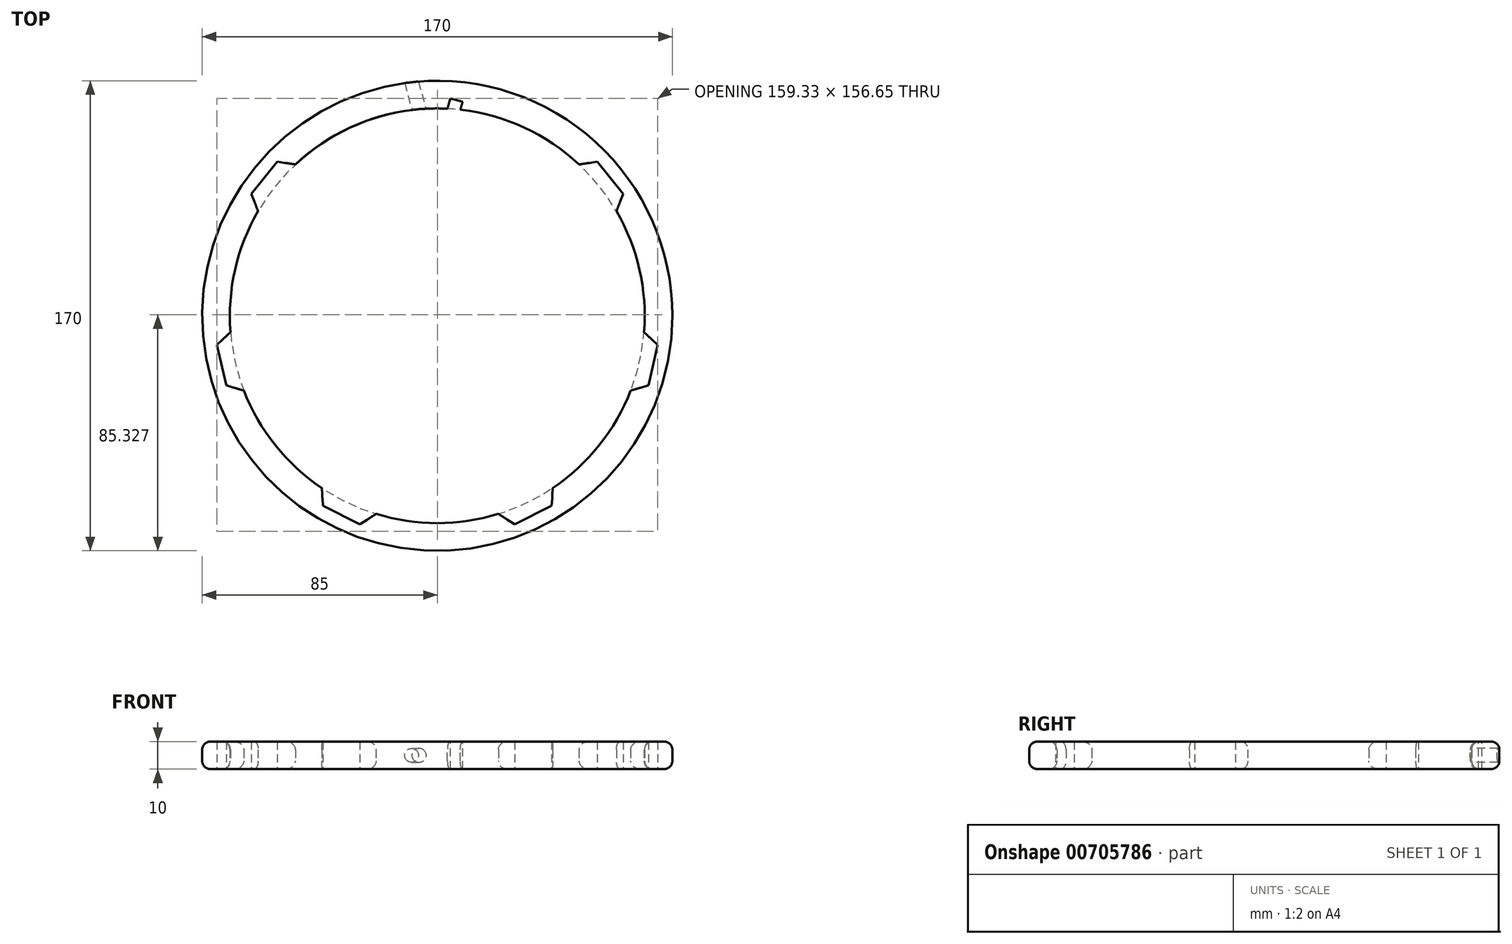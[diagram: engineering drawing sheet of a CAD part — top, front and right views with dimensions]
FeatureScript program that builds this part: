
annotation { "Feature Type Name" : "Feature", "Feature Type Description" : "" }
export const myFeature = defineFeature(function(context is Context, id is Id, definition is map)
    precondition{}
    {
        {
            var Q0;
            Q0=qCreatedBy(makeId("Top.planeOp"),FACE);
            var sketch = newSketch(context, id + "F0", { "sketchPlane" : qUnion([Q0])});
            skCircle(sketch, "E0", {"center": v(0, 0) * mm, "radius": 85 * mm});
            skCircle(sketch, "E1.0", {"center": v(0, 0) * mm, "radius": 75 * mm});
            skPoint(sketch, "E2", {"position": v(0, 80) * mm});
            skPoint(sketch, "E3.1.1", {"position": v(-62.55, 49.88) * mm});
            skPoint(sketch, "E3.2.1", {"position": v(-78, -17.8) * mm});
            skPoint(sketch, "E3.3.1", {"position": v(-34.71, -72.08) * mm});
            skPoint(sketch, "E3.4.1", {"position": v(34.71, -72.08) * mm});
            skPoint(sketch, "E3.5.1", {"position": v(78, -17.8) * mm});
            skPoint(sketch, "E3.6.1", {"position": v(62.55, 49.88) * mm});
            skPoint(sketch, "E4", {"position": v(-7.48, 80) * mm});
            skPoint(sketch, "E5.MirrorP", {"position": v(7.48, 80) * mm});
            skLineSegment(sketch, "E6", {"start": v(-7.48, 80) * mm, "end": v(34.71, -72.08) * mm, "construction": true});
            skLineSegment(sketch, "E7", {"start": v(34.71, -72.08) * mm, "end": v(-62.55, 49.88) * mm, "construction": true});
            skLineSegment(sketch, "E8", {"start": v(-62.55, 49.88) * mm, "end": v(78, -17.8) * mm, "construction": true});
            skLineSegment(sketch, "E9", {"start": v(78, -17.8) * mm, "end": v(-78, -17.8) * mm, "construction": true});
            skLineSegment(sketch, "E10", {"start": v(-78, -17.8) * mm, "end": v(62.55, 49.88) * mm, "construction": true});
            skLineSegment(sketch, "E11", {"start": v(62.55, 49.88) * mm, "end": v(-34.71, -72.08) * mm, "construction": true});
            skLineSegment(sketch, "E12", {"start": v(-34.71, -72.08) * mm, "end": v(7.48, 80) * mm, "construction": true});
            skCircle(sketch, "E13", {"center": v(34.71, -72.08) * mm, "radius": 23.6 * mm, "construction": true});
            skCircle(sketch, "E14", {"center": v(78, -17.8) * mm, "radius": 25.74 * mm, "construction": true});
            skLineSegment(sketch, "E15", {"start": v(54.8, -6.63) * mm, "end": v(52.26, -17.8) * mm, "construction": true});
            skLineSegment(sketch, "E16", {"start": v(76.33, -25.11) * mm, "end": v(79.66, -10.49) * mm});
            skLineSegment(sketch, "E17", {"start": v(57.87, 55.74) * mm, "end": v(67.22, 44.02) * mm});
            skCircle(sketch, "E18", {"center": v(62.55, 49.88) * mm, "radius": 21.8 * mm, "construction": true});
            skLineSegment(sketch, "E19", {"start": v(48.95, 32.83) * mm, "end": v(42.9, 40.42) * mm, "construction": true});
            skLineSegment(sketch, "E20", {"start": v(78, -17.8) * mm, "end": v(55.94, -12.77) * mm, "construction": true});
            skLineSegment(sketch, "E21", {"start": v(79.66, -10.49) * mm, "end": v(74.76, -5.94) * mm});
            skLineSegment(sketch, "E22.MirrorCS", {"start": v(76.33, -25.11) * mm, "end": v(69.94, -27.08) * mm});
            skLineSegment(sketch, "E23", {"start": v(62.55, 49.88) * mm, "end": v(49.56, 39.52) * mm, "construction": true});
            skLineSegment(sketch, "E24", {"start": v(57.87, 55.74) * mm, "end": v(51.26, 54.75) * mm});
            skLineSegment(sketch, "E25.MirrorCS", {"start": v(67.22, 44.02) * mm, "end": v(64.78, 37.8) * mm});
            skLineSegment(sketch, "E26.MirrorCS", {"start": v(-57.87, 55.74) * mm, "end": v(-51.26, 54.75) * mm});
            skLineSegment(sketch, "E27.MirrorCS", {"start": v(-57.87, 55.74) * mm, "end": v(-67.22, 44.02) * mm});
            skLineSegment(sketch, "E28.MirrorCS", {"start": v(-67.22, 44.02) * mm, "end": v(-64.78, 37.8) * mm});
            skLineSegment(sketch, "E29.MirrorCS", {"start": v(-79.66, -10.49) * mm, "end": v(-74.76, -5.94) * mm});
            skLineSegment(sketch, "E30.MirrorCS", {"start": v(-76.33, -25.11) * mm, "end": v(-79.66, -10.49) * mm});
            skLineSegment(sketch, "E31.MirrorCS", {"start": v(-76.33, -25.11) * mm, "end": v(-69.94, -27.08) * mm});
            skLineSegment(sketch, "E32", {"start": v(20, -53.62) * mm, "end": v(28.4, -49.33) * mm});
            skLineSegment(sketch, "E33", {"start": v(28.03, -75.49) * mm, "end": v(41.4, -68.67) * mm});
            skLineSegment(sketch, "E34", {"start": v(34.71, -72.08) * mm, "end": v(27.95, -58.84) * mm, "construction": true});
            skLineSegment(sketch, "E35", {"start": v(41.4, -68.67) * mm, "end": v(41.72, -62.33) * mm});
            skLineSegment(sketch, "E36", {"start": v(28.03, -75.49) * mm, "end": v(22.13, -71.66) * mm});
            skLineSegment(sketch, "E37.MirrorCS", {"start": v(-41.4, -68.67) * mm, "end": v(-41.72, -62.33) * mm});
            skLineSegment(sketch, "E38.MirrorCS", {"start": v(-28.03, -75.49) * mm, "end": v(-41.4, -68.67) * mm});
            skLineSegment(sketch, "E39.MirrorCS", {"start": v(-28.03, -75.49) * mm, "end": v(-22.13, -71.66) * mm});
            skSolve(sketch);
        }
        {
            var Q0;
            Q0 = qSketchRegion(id + "F0", true);
            extrude(context, id + "F1", {"entities" : qUnion([Q0]), "depth" : 10 * mm, "offsetDistance" : 25 * mm});
        }
        {
            var Q0;
            Q0=sQuery(id+"F0.wireOp",VERTEX,"E6.start");
            var Q1;
            Q1=sQuery(id+"F0.wireOp",EDGE,"E6");
            cPlane(context, id + "F2", {"entities" : qUnion([Q0, Q1]), "cplaneType" : CPlaneType.LINE_POINT, "offset" : 25 * mm, "width" : 150 * mm, "height" : 150 * mm});
        }
        {
            var Q0;
            Q0=qCreatedBy(id+"F2.planeOp",FACE);
            var sketch = newSketch(context, id + "F3", { "sketchPlane" : qUnion([Q0])});
            skCircle(sketch, "E40", {"center": v(13.62, 5) * mm, "radius": 2.5 * mm});
            skLineSegment(sketch, "E41.0", {"start": v(-85, 0) * mm, "end": v(85, 0) * mm});
            skLineSegment(sketch, "E42.0", {"start": v(-85, 10) * mm, "end": v(85, 10) * mm});
            skLineSegment(sketch, "E43", {"start": v(13.62, 0) * mm, "end": v(13.62, 5) * mm, "construction": true});
            skLineSegment(sketch, "E44", {"start": v(13.62, 5) * mm, "end": v(13.62, 10) * mm, "construction": true});
            skSolve(sketch);
        }
        {
            var Q0;
            Q0 = qSketchRegion(id + "F3", true);
            extrude(context, id + "F4", {"entities" : qUnion([Q0]), "operationType" : NewBodyOperationType.REMOVE, "endBound" : BoundingType.UP_TO_NEXT, "oppositeDirection" : true, "depth" : 25 * mm, "offsetDistance" : 25 * mm, "hasSecondDirection" : true, "secondDirectionBound" : SecondDirectionBoundingType.UP_TO_NEXT, "secondDirectionOppositeDirection" : false, "secondDirectionDepth" : 25 * mm});
        }
        {
            var Q0;
            Q0=sQuery(id+"F0.wireOp",VERTEX,"E5.MirrorP");
            var Q1;
            Q1=sQuery(id+"F0.wireOp",EDGE,"E12");
            cPlane(context, id + "F5", {"entities" : qUnion([Q0, Q1]), "cplaneType" : CPlaneType.LINE_POINT, "offset" : 25 * mm, "width" : 150 * mm, "height" : 150 * mm});
        }
        {
            var Q0;
            Q0=makeQuery(id+"F1.opExtrude","CAP_FACE",FACE,{"disambiguationData":[OSD([sQuery(id+"F0.wireOp",EDGE,"E0"),sQuery(id+"F0.wireOp",EDGE,"E1.0"),sQuery(id+"F0.wireOp",EDGE,"E16"),sQuery(id+"F0.wireOp",EDGE,"E17"),sQuery(id+"F0.wireOp",EDGE,"E21"),sQuery(id+"F0.wireOp",EDGE,"E22.MirrorCS"),sQuery(id+"F0.wireOp",EDGE,"E24"),sQuery(id+"F0.wireOp",EDGE,"E25.MirrorCS"),sQuery(id+"F0.wireOp",EDGE,"E26.MirrorCS"),sQuery(id+"F0.wireOp",EDGE,"E27.MirrorCS"),sQuery(id+"F0.wireOp",EDGE,"E28.MirrorCS"),sQuery(id+"F0.wireOp",EDGE,"E29.MirrorCS"),sQuery(id+"F0.wireOp",EDGE,"E30.MirrorCS"),sQuery(id+"F0.wireOp",EDGE,"E31.MirrorCS"),sQuery(id+"F0.wireOp",EDGE,"E33"),sQuery(id+"F0.wireOp",EDGE,"E35"),sQuery(id+"F0.wireOp",EDGE,"E36"),sQuery(id+"F0.wireOp",EDGE,"E37.MirrorCS"),sQuery(id+"F0.wireOp",EDGE,"E38.MirrorCS"),sQuery(id+"F0.wireOp",EDGE,"E39.MirrorCS")])],"isStart":false});
            var sketch = newSketch(context, id + "F6", { "sketchPlane" : qUnion([Q0])});
            skLineSegment(sketch, "E45", {"start": v(-11.54, 85.28) * mm, "end": v(31.77, 73.26) * mm});
            skLineSegment(sketch, "E46", {"start": v(3.68, 74.9) * mm, "end": v(5.27, 80.61) * mm});
            skLineSegment(sketch, "E47.0", {"start": v(-34.71, -72.08) * mm, "end": v(7.48, 80) * mm});
            skLineSegment(sketch, "E48.MirrorCS", {"start": v(8.35, 74.53) * mm, "end": v(9.7, 79.39) * mm});
            skLineSegment(sketch, "E49", {"start": v(4.72, 78.65) * mm, "end": v(9.15, 77.42) * mm});
            skSolve(sketch);
        }
        {
            var Q0;
            {var subQ0=sQuery(id+"F6.wireOp",EDGE,"E49");var subQ6=sQuery(id+"F6.wireOp",EDGE,"E48.MirrorCS");var subQ7=makeQuery(id+"F6.imprint","INTERSECT",VERTEX,{"derivedFrom":[subQ6,subQ0]});Q0=makeQuery(id+"F6.imprint","IMPRINT",FACE,{"disambiguationData":[TD([[makeQuery(id+"F6.imprint","IMPRINT",EDGE,{"disambiguationData":[TD([[subQ7,1.0]])],"derivedFrom":subQ0}),-1.0]])]});}
            var Q1;
            {var subQ0=sQuery(id+"F6.wireOp",EDGE,"E46");var subQ4=sQuery(id+"F6.wireOp",EDGE,"E49");var subQ5=makeQuery(id+"F6.imprint","INTERSECT",VERTEX,{"derivedFrom":[subQ0,subQ4]});Q1=makeQuery(id+"F6.imprint","IMPRINT",FACE,{"disambiguationData":[TD([[makeQuery(id+"F6.imprint","IMPRINT",EDGE,{"disambiguationData":[TD([[subQ5,-1.0]])],"derivedFrom":subQ4}),-1.0]])]});}
            extrude(context, id + "F7", {"entities" : qUnion([Q0, Q1]), "operationType" : NewBodyOperationType.REMOVE, "endBound" : BoundingType.UP_TO_NEXT, "oppositeDirection" : true, "depth" : 25 * mm, "offsetDistance" : 25 * mm});
        }
        {
            var Q0;
            {var subQ0=sQuery(id+"F0.wireOp",EDGE,"E26.MirrorCS");var subQ1=sQuery(id+"F0.wireOp",EDGE,"E24");var subQ2=sQuery(id+"F0.wireOp",EDGE,"E1.0");var subQ3=makeQuery(id+"F0.imprint","IMPRINT",EDGE,{"disambiguationData":[TD([[makeQuery(id+"F0.imprint","INTERSECT",VERTEX,{"derivedFrom":[subQ2,subQ1]}),-1.0]])],"derivedFrom":subQ2});Q0=makeQuery(id+"F7.boolean.opBoolean","SPLIT",EDGE,{"disambiguationData":[TD([makeQuery(id+"F1.opExtrude","SWEPT_FACE",FACE,{"disambiguationData":[OSD([subQ0])]})])],"derivedFrom":makeQuery(id+"F1.opExtrude","CAP_EDGE",EDGE,{"disambiguationData":[OSD([subQ2]),TDD([subQ3])],"isStart":false})});}
            var Q1;
            {var subQ0=sQuery(id+"F0.wireOp",EDGE,"E1.0");Q1=makeQuery(id+"F1.opExtrude","CAP_EDGE",EDGE,{"disambiguationData":[OSD([subQ0]),TDD([makeQuery(id+"F0.imprint","IMPRINT",EDGE,{"disambiguationData":[TD([[makeQuery(id+"F0.imprint","INTERSECT",VERTEX,{"derivedFrom":[subQ0,sQuery(id+"F0.wireOp",EDGE,"E21")]}),-1.0]])],"derivedFrom":subQ0})])],"isStart":false});}
            var Q2;
            {var subQ0=sQuery(id+"F0.wireOp",EDGE,"E1.0");Q2=makeQuery(id+"F1.opExtrude","CAP_EDGE",EDGE,{"disambiguationData":[OSD([subQ0]),TDD([makeQuery(id+"F0.imprint","IMPRINT",EDGE,{"disambiguationData":[TD([[makeQuery(id+"F0.imprint","INTERSECT",VERTEX,{"derivedFrom":[subQ0,sQuery(id+"F0.wireOp",EDGE,"E22.MirrorCS")]}),1.0]])],"derivedFrom":subQ0})])],"isStart":false});}
            var Q3;
            {var subQ0=sQuery(id+"F0.wireOp",EDGE,"E1.0");Q3=makeQuery(id+"F1.opExtrude","CAP_EDGE",EDGE,{"disambiguationData":[OSD([subQ0]),TDD([makeQuery(id+"F0.imprint","IMPRINT",EDGE,{"disambiguationData":[TD([[makeQuery(id+"F0.imprint","INTERSECT",VERTEX,{"derivedFrom":[subQ0,sQuery(id+"F0.wireOp",EDGE,"E36")]}),1.0]])],"derivedFrom":subQ0})])],"isStart":false});}
            var Q4;
            {var subQ0=sQuery(id+"F0.wireOp",EDGE,"E1.0");Q4=makeQuery(id+"F1.opExtrude","CAP_EDGE",EDGE,{"disambiguationData":[OSD([subQ0]),TDD([makeQuery(id+"F0.imprint","IMPRINT",EDGE,{"disambiguationData":[TD([[makeQuery(id+"F0.imprint","INTERSECT",VERTEX,{"derivedFrom":[subQ0,sQuery(id+"F0.wireOp",EDGE,"E31.MirrorCS")]}),-1.0]])],"derivedFrom":subQ0})])],"isStart":false});}
            var Q5;
            {var subQ0=sQuery(id+"F0.wireOp",EDGE,"E1.0");Q5=makeQuery(id+"F1.opExtrude","CAP_EDGE",EDGE,{"disambiguationData":[OSD([subQ0]),TDD([makeQuery(id+"F0.imprint","IMPRINT",EDGE,{"disambiguationData":[TD([[makeQuery(id+"F0.imprint","INTERSECT",VERTEX,{"derivedFrom":[subQ0,sQuery(id+"F0.wireOp",EDGE,"E28.MirrorCS")]}),-1.0]])],"derivedFrom":subQ0})])],"isStart":false});}
            var Q6;
            Q6=makeQuery(id+"F1.opExtrude","CAP_EDGE",EDGE,{"disambiguationData":[OSD([sQuery(id+"F0.wireOp",EDGE,"E0")])],"isStart":false});
            var Q7;
            {var subQ1=sQuery(id+"F0.wireOp",EDGE,"E24");var subQ2=sQuery(id+"F0.wireOp",EDGE,"E1.0");var subQ3=makeQuery(id+"F0.imprint","IMPRINT",EDGE,{"disambiguationData":[TD([[makeQuery(id+"F0.imprint","INTERSECT",VERTEX,{"derivedFrom":[subQ2,subQ1]}),-1.0]])],"derivedFrom":subQ2});Q7=makeQuery(id+"F7.boolean.opBoolean","SPLIT",EDGE,{"disambiguationData":[TD([makeQuery(id+"F1.opExtrude","SWEPT_FACE",FACE,{"disambiguationData":[OSD([subQ1])]})])],"derivedFrom":makeQuery(id+"F1.opExtrude","CAP_EDGE",EDGE,{"disambiguationData":[OSD([subQ2]),TDD([subQ3])],"isStart":false})});}
            var Q8;
            Q8=makeQuery(id+"F1.opExtrude","CAP_EDGE",EDGE,{"disambiguationData":[OSD([sQuery(id+"F0.wireOp",EDGE,"E0")])],"isStart":true});
            var Q9;
            {var subQ0=sQuery(id+"F0.wireOp",EDGE,"E1.0");Q9=makeQuery(id+"F1.opExtrude","CAP_EDGE",EDGE,{"disambiguationData":[OSD([subQ0]),TDD([makeQuery(id+"F0.imprint","IMPRINT",EDGE,{"disambiguationData":[TD([[makeQuery(id+"F0.imprint","INTERSECT",VERTEX,{"derivedFrom":[subQ0,sQuery(id+"F0.wireOp",EDGE,"E31.MirrorCS")]}),-1.0]])],"derivedFrom":subQ0})])],"isStart":true});}
            var Q10;
            {var subQ0=sQuery(id+"F0.wireOp",EDGE,"E1.0");Q10=makeQuery(id+"F1.opExtrude","CAP_EDGE",EDGE,{"disambiguationData":[OSD([subQ0]),TDD([makeQuery(id+"F0.imprint","IMPRINT",EDGE,{"disambiguationData":[TD([[makeQuery(id+"F0.imprint","INTERSECT",VERTEX,{"derivedFrom":[subQ0,sQuery(id+"F0.wireOp",EDGE,"E36")]}),1.0]])],"derivedFrom":subQ0})])],"isStart":true});}
            var Q11;
            {var subQ0=sQuery(id+"F0.wireOp",EDGE,"E1.0");Q11=makeQuery(id+"F1.opExtrude","CAP_EDGE",EDGE,{"disambiguationData":[OSD([subQ0]),TDD([makeQuery(id+"F0.imprint","IMPRINT",EDGE,{"disambiguationData":[TD([[makeQuery(id+"F0.imprint","INTERSECT",VERTEX,{"derivedFrom":[subQ0,sQuery(id+"F0.wireOp",EDGE,"E22.MirrorCS")]}),1.0]])],"derivedFrom":subQ0})])],"isStart":true});}
            var Q12;
            {var subQ0=sQuery(id+"F0.wireOp",EDGE,"E1.0");Q12=makeQuery(id+"F1.opExtrude","CAP_EDGE",EDGE,{"disambiguationData":[OSD([subQ0]),TDD([makeQuery(id+"F0.imprint","IMPRINT",EDGE,{"disambiguationData":[TD([[makeQuery(id+"F0.imprint","INTERSECT",VERTEX,{"derivedFrom":[subQ0,sQuery(id+"F0.wireOp",EDGE,"E21")]}),-1.0]])],"derivedFrom":subQ0})])],"isStart":true});}
            var Q13;
            {var subQ1=sQuery(id+"F0.wireOp",EDGE,"E24");var subQ2=sQuery(id+"F0.wireOp",EDGE,"E1.0");var subQ3=makeQuery(id+"F0.imprint","IMPRINT",EDGE,{"disambiguationData":[TD([[makeQuery(id+"F0.imprint","INTERSECT",VERTEX,{"derivedFrom":[subQ2,subQ1]}),-1.0]])],"derivedFrom":subQ2});Q13=makeQuery(id+"F7.boolean.opBoolean","SPLIT",EDGE,{"disambiguationData":[TD([makeQuery(id+"F1.opExtrude","SWEPT_FACE",FACE,{"disambiguationData":[OSD([subQ1])]})])],"derivedFrom":makeQuery(id+"F1.opExtrude","CAP_EDGE",EDGE,{"disambiguationData":[OSD([subQ2]),TDD([subQ3])],"isStart":true})});}
            var Q14;
            {var subQ0=sQuery(id+"F0.wireOp",EDGE,"E26.MirrorCS");var subQ1=sQuery(id+"F0.wireOp",EDGE,"E24");var subQ2=sQuery(id+"F0.wireOp",EDGE,"E1.0");var subQ3=makeQuery(id+"F0.imprint","IMPRINT",EDGE,{"disambiguationData":[TD([[makeQuery(id+"F0.imprint","INTERSECT",VERTEX,{"derivedFrom":[subQ2,subQ1]}),-1.0]])],"derivedFrom":subQ2});Q14=makeQuery(id+"F7.boolean.opBoolean","SPLIT",EDGE,{"disambiguationData":[TD([makeQuery(id+"F1.opExtrude","SWEPT_FACE",FACE,{"disambiguationData":[OSD([subQ0])]})])],"derivedFrom":makeQuery(id+"F1.opExtrude","CAP_EDGE",EDGE,{"disambiguationData":[OSD([subQ2]),TDD([subQ3])],"isStart":true})});}
            var Q15;
            {var subQ0=sQuery(id+"F0.wireOp",EDGE,"E1.0");Q15=makeQuery(id+"F1.opExtrude","CAP_EDGE",EDGE,{"disambiguationData":[OSD([subQ0]),TDD([makeQuery(id+"F0.imprint","IMPRINT",EDGE,{"disambiguationData":[TD([[makeQuery(id+"F0.imprint","INTERSECT",VERTEX,{"derivedFrom":[subQ0,sQuery(id+"F0.wireOp",EDGE,"E28.MirrorCS")]}),-1.0]])],"derivedFrom":subQ0})])],"isStart":true});}
            fillet(context, id + "F8", {"entities" : qUnion([Q0, Q1, Q2, Q3, Q4, Q5, Q6, Q7, Q8, Q9, Q10, Q11, Q12, Q13, Q14, Q15]), "radius" : 3 * mm, "tangentPropagation" : true, "allowEdgeOverflow" : false});
        }
    });
